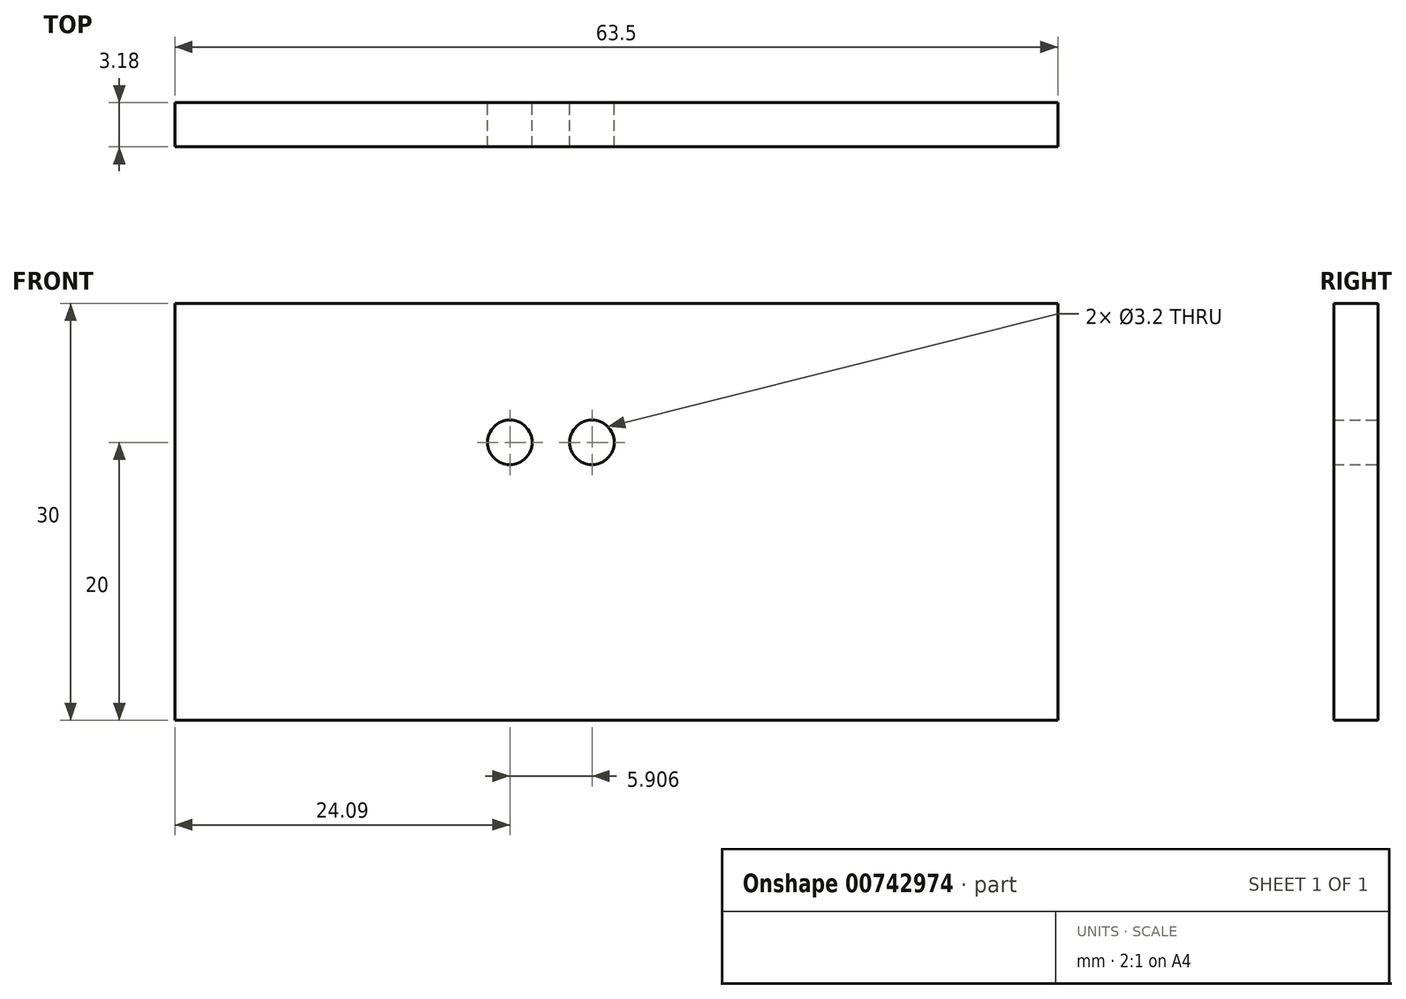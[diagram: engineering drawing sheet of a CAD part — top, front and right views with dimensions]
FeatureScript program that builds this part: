
annotation { "Feature Type Name" : "Feature", "Feature Type Description" : "" }
export const myFeature = defineFeature(function(context is Context, id is Id, definition is map)
    precondition{}
    {
        {
            var Q0;
            Q0=qCreatedBy(makeId("Front.planeOp"),FACE);
            var sketch = newSketch(context, id + "F0", { "sketchPlane" : qUnion([Q0])});
            skLineSegment(sketch, "E0.bottom", {"start": v(-30.88, 10) * mm, "end": v(32.62, 10) * mm});
            skLineSegment(sketch, "E0.top", {"start": v(-30.88, -20) * mm, "end": v(32.62, -20) * mm});
            skLineSegment(sketch, "E0.left", {"start": v(-30.88, 10) * mm, "end": v(-30.88, -20) * mm});
            skLineSegment(sketch, "E0.right", {"start": v(32.62, 10) * mm, "end": v(32.62, -20) * mm});
            skLineSegment(sketch, "E1", {"start": v(-30.88, -20) * mm, "end": v(-30.88, 0) * mm});
            skCircle(sketch, "E2", {"center": v(-0.88, 0) * mm, "radius": 1.6 * mm});
            skCircle(sketch, "E3", {"center": v(-6.79, 0) * mm, "radius": 1.6 * mm});
            skSolve(sketch);
        }
        {
            var Q0;
            Q0=makeQuery(id+"F0.imprint","IMPRINT",FACE,{"disambiguationData":[TD([[makeQuery(id+"F0.imprint","IMPRINT",EDGE,{"derivedFrom":sQuery(id+"F0.wireOp",EDGE,"E0.bottom")}),-1.0]])]});
            extrude(context, id + "F1", {"entities" : qUnion([Q0]), "depth" : 3.17 * mm, "offsetDistance" : 25.4 * mm});
        }
    });
